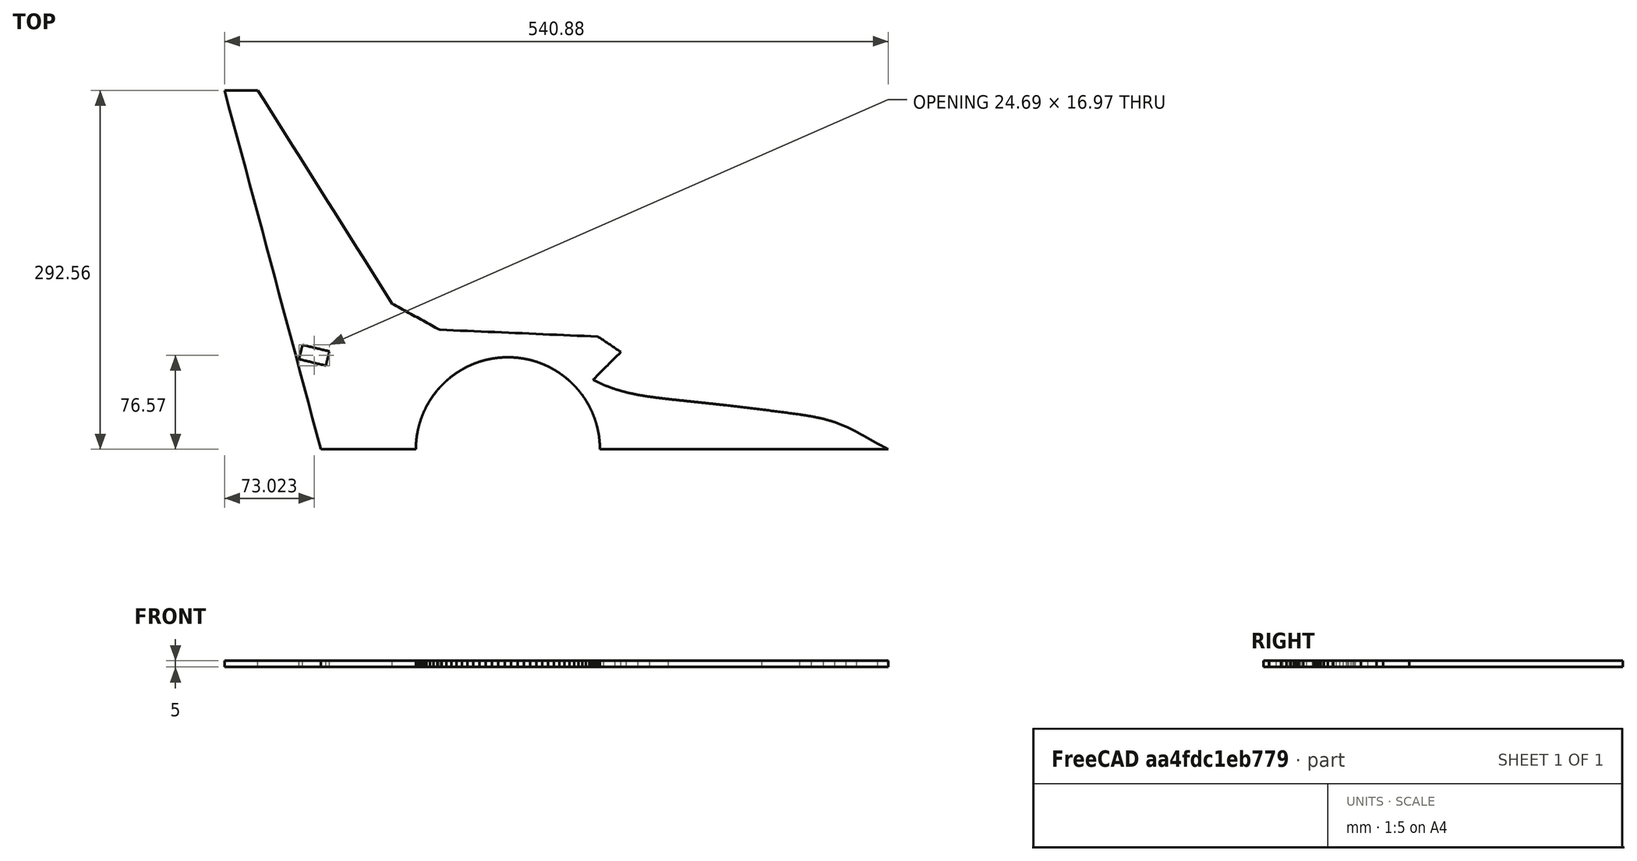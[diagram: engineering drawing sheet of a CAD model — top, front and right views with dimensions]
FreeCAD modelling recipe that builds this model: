
FCSTD DOCUMENT  (FreeCAD 0.19R)
Label: F-35_v2_parts_3
License: All rights reserved
LicenseURL: http://en.wikipedia.org/wiki/All_rights_reserved
objects: App::DocumentObjectGroup×2, PartDesign::CoordinateSystem×2, App::FeaturePython×1, Sketcher::SketchObject×1, PartDesign::Pad×1, PartDesign::Body×1, App::Part×1
note: 6 computed .brp shape members not serialized (recipe doc carries the construction recipe); baked Part::Feature solids carry a one-line shape summary decoded from their .brp

FEATURE [App::DocumentObjectGroup] Parts
FEATURE [PartDesign::CoordinateSystem] LCS_Origin
  AttacherType = Attacher::AttachEngine3D
  MapMode = 2
  Support = -> [X_Axis]
FEATURE [App::DocumentObjectGroup] Constraints
FEATURE [App::FeaturePython] Variables  # WARN: FeaturePython — macro-defined, semantics opaque (R4)
FEATURE [Sketcher::SketchObject] Sketch002
  FullyConstrained = false
  sketch-geometry (77):
    g0: BSplineCurve PolesCount=2 KnotsCount=2 Degree=1 IsPeriodic=0
    g1: BSplineCurve PolesCount=2 KnotsCount=2 Degree=1 IsPeriodic=0
    g2: BSplineCurve PolesCount=2 KnotsCount=2 Degree=1 IsPeriodic=0
    g3: BSplineCurve PolesCount=2 KnotsCount=2 Degree=1 IsPeriodic=0
    g4: BSplineCurve PolesCount=2 KnotsCount=2 Degree=1 IsPeriodic=0
    g5: BSplineCurve PolesCount=2 KnotsCount=2 Degree=1 IsPeriodic=0
    g6: BSplineCurve PolesCount=2 KnotsCount=2 Degree=1 IsPeriodic=0
    g7: BSplineCurve PolesCount=2 KnotsCount=2 Degree=1 IsPeriodic=0
    g8: BSplineCurve PolesCount=2 KnotsCount=2 Degree=1 IsPeriodic=0
    g9: BSplineCurve PolesCount=2 KnotsCount=2 Degree=1 IsPeriodic=0
    g10: BSplineCurve PolesCount=2 KnotsCount=2 Degree=1 IsPeriodic=0
    g11: BSplineCurve PolesCount=2 KnotsCount=2 Degree=1 IsPeriodic=0
    g12: BSplineCurve PolesCount=2 KnotsCount=2 Degree=1 IsPeriodic=0
    g13: BSplineCurve PolesCount=2 KnotsCount=2 Degree=1 IsPeriodic=0
    g14: BSplineCurve PolesCount=2 KnotsCount=2 Degree=1 IsPeriodic=0
    g15: BSplineCurve PolesCount=2 KnotsCount=2 Degree=1 IsPeriodic=0
    g16: BSplineCurve PolesCount=2 KnotsCount=2 Degree=1 IsPeriodic=0
    g17: BSplineCurve PolesCount=2 KnotsCount=2 Degree=1 IsPeriodic=0
    g18: BSplineCurve PolesCount=2 KnotsCount=2 Degree=1 IsPeriodic=0
    g19: BSplineCurve PolesCount=2 KnotsCount=2 Degree=1 IsPeriodic=0
    g20: BSplineCurve PolesCount=2 KnotsCount=2 Degree=1 IsPeriodic=0
    g21: BSplineCurve PolesCount=2 KnotsCount=2 Degree=1 IsPeriodic=0
    g22: BSplineCurve PolesCount=2 KnotsCount=2 Degree=1 IsPeriodic=0
    g23: BSplineCurve PolesCount=2 KnotsCount=2 Degree=1 IsPeriodic=0
    g24: BSplineCurve PolesCount=2 KnotsCount=2 Degree=1 IsPeriodic=0
    g25: BSplineCurve PolesCount=2 KnotsCount=2 Degree=1 IsPeriodic=0
    g26: BSplineCurve PolesCount=2 KnotsCount=2 Degree=1 IsPeriodic=0
    g27: BSplineCurve PolesCount=2 KnotsCount=2 Degree=1 IsPeriodic=0
    g28: BSplineCurve PolesCount=2 KnotsCount=2 Degree=1 IsPeriodic=0
    g29: BSplineCurve PolesCount=2 KnotsCount=2 Degree=1 IsPeriodic=0
    g30: BSplineCurve PolesCount=2 KnotsCount=2 Degree=1 IsPeriodic=0
    g31: BSplineCurve PolesCount=2 KnotsCount=2 Degree=1 IsPeriodic=0
    g32: BSplineCurve PolesCount=2 KnotsCount=2 Degree=1 IsPeriodic=0
    g33: BSplineCurve PolesCount=2 KnotsCount=2 Degree=1 IsPeriodic=0
    g34: BSplineCurve PolesCount=2 KnotsCount=2 Degree=1 IsPeriodic=0
    g35: BSplineCurve PolesCount=2 KnotsCount=2 Degree=1 IsPeriodic=0
    g36: BSplineCurve PolesCount=2 KnotsCount=2 Degree=1 IsPeriodic=0
    g37: BSplineCurve PolesCount=2 KnotsCount=2 Degree=1 IsPeriodic=0
    g38: BSplineCurve PolesCount=2 KnotsCount=2 Degree=1 IsPeriodic=0
    g39: BSplineCurve PolesCount=2 KnotsCount=2 Degree=1 IsPeriodic=0
    g40: BSplineCurve PolesCount=2 KnotsCount=2 Degree=1 IsPeriodic=0
    g41: BSplineCurve PolesCount=2 KnotsCount=2 Degree=1 IsPeriodic=0
    g42: BSplineCurve PolesCount=2 KnotsCount=2 Degree=1 IsPeriodic=0
    g43: BSplineCurve PolesCount=2 KnotsCount=2 Degree=1 IsPeriodic=0
    g44: BSplineCurve PolesCount=2 KnotsCount=2 Degree=1 IsPeriodic=0
    g45: BSplineCurve PolesCount=2 KnotsCount=2 Degree=1 IsPeriodic=0
    g46: BSplineCurve PolesCount=2 KnotsCount=2 Degree=1 IsPeriodic=0
    g47: BSplineCurve PolesCount=2 KnotsCount=2 Degree=1 IsPeriodic=0
    g48: BSplineCurve PolesCount=2 KnotsCount=2 Degree=1 IsPeriodic=0
    g49: BSplineCurve PolesCount=2 KnotsCount=2 Degree=1 IsPeriodic=0
    g50: BSplineCurve PolesCount=2 KnotsCount=2 Degree=1 IsPeriodic=0
    g51: BSplineCurve PolesCount=2 KnotsCount=2 Degree=1 IsPeriodic=0
    g52: BSplineCurve PolesCount=2 KnotsCount=2 Degree=1 IsPeriodic=0
    g53: BSplineCurve PolesCount=2 KnotsCount=2 Degree=1 IsPeriodic=0
    g54: BSplineCurve PolesCount=2 KnotsCount=2 Degree=1 IsPeriodic=0
    g55: BSplineCurve PolesCount=2 KnotsCount=2 Degree=1 IsPeriodic=0
    g56: BSplineCurve PolesCount=2 KnotsCount=2 Degree=1 IsPeriodic=0
    g57: BSplineCurve PolesCount=2 KnotsCount=2 Degree=1 IsPeriodic=0
    g58: BSplineCurve PolesCount=2 KnotsCount=2 Degree=1 IsPeriodic=0
    g59: BSplineCurve PolesCount=2 KnotsCount=2 Degree=1 IsPeriodic=0
    g60: BSplineCurve PolesCount=2 KnotsCount=2 Degree=1 IsPeriodic=0
    g61: BSplineCurve PolesCount=2 KnotsCount=2 Degree=1 IsPeriodic=0
    g62: BSplineCurve PolesCount=2 KnotsCount=2 Degree=1 IsPeriodic=0
    g63: BSplineCurve PolesCount=2 KnotsCount=2 Degree=1 IsPeriodic=0
    g64: BSplineCurve PolesCount=2 KnotsCount=2 Degree=1 IsPeriodic=0
    g65: BSplineCurve PolesCount=2 KnotsCount=2 Degree=1 IsPeriodic=0
    g66: BSplineCurve PolesCount=2 KnotsCount=2 Degree=1 IsPeriodic=0
    g67: BSplineCurve PolesCount=2 KnotsCount=2 Degree=1 IsPeriodic=0
    g68: BSplineCurve PolesCount=2 KnotsCount=2 Degree=1 IsPeriodic=0
    g69: BSplineCurve PolesCount=2 KnotsCount=2 Degree=1 IsPeriodic=0
    g70: BSplineCurve PolesCount=2 KnotsCount=2 Degree=1 IsPeriodic=0
    g71: BSplineCurve PolesCount=2 KnotsCount=2 Degree=1 IsPeriodic=0
    g72: BSplineCurve PolesCount=2 KnotsCount=2 Degree=1 IsPeriodic=0
    g73: BSplineCurve PolesCount=2 KnotsCount=2 Degree=1 IsPeriodic=0
    g74: BSplineCurve PolesCount=2 KnotsCount=2 Degree=1 IsPeriodic=0
    g75: BSplineCurve PolesCount=2 KnotsCount=2 Degree=1 IsPeriodic=0
    g76: BSplineCurve PolesCount=2 KnotsCount=2 Degree=1 IsPeriodic=0
  constraints (62):
    c: Coincident(g6,g7)
    c: Coincident(g7,g8)
    c: Coincident(g8,g9)
    c: Coincident(g9,g10)
    c: Coincident(g10,g11)
    c: Coincident(g11,g12)
    c: Coincident(g12,g13)
    c: Coincident(g13,g14)
    c: Coincident(g14,g15)
    c: Coincident(g15,g16)
    c: Coincident(g16,g17)
    c: Coincident(g17,g18)
    c: Coincident(g18,g19)
    c: Coincident(g19,g20)
    c: Coincident(g20,g21)
    c: Coincident(g21,g22)
    c: Coincident(g22,g23)
    c: Coincident(g23,g24)
    c: Coincident(g25,g26)
    c: Coincident(g26,g27)
    c: Coincident(g27,g28)
    c: Coincident(g28,g29)
    c: Coincident(g29,g30)
    c: Coincident(g30,g31)
    c: Coincident(g31,g32)
    c: Coincident(g32,g33)
    c: Coincident(g33,g34)
    c: Coincident(g34,g35)
    c: Coincident(g35,g36)
    c: Coincident(g36,g37)
    c: Coincident(g37,g38)
    c: Coincident(g38,g39)
    c: Coincident(g39,g40)
    c: Coincident(g40,g41)
    c: Coincident(g41,g42)
    c: Coincident(g42,g43)
    c: Coincident(g43,g44)
    c: Coincident(g44,g45)
    c: Coincident(g45,g46)
    c: Coincident(g46,g47)
    c: Coincident(g47,g48)
    c: Coincident(g48,g49)
    c: Coincident(g49,g50)
    c: Coincident(g50,g51)
    c: Coincident(g51,g52)
    c: Coincident(g52,g53)
    c: Coincident(g53,g54)
    c: Coincident(g54,g55)
    c: Coincident(g55,g56)
    c: Coincident(g56,g57)
    c: Coincident(g57,g58)
    c: Coincident(g58,g59)
    c: Coincident(g59,g60)
    c: Coincident(g60,g61)
    c: Coincident(g61,g62)
    c: Coincident(g62,g63)
    c: Coincident(g63,g64)
    c: Coincident(g64,g65)
    c: Coincident(g65,g66)
    c: Coincident(g66,g67)
    c: Coincident(g67,g68)
    c: Coincident(g68,g69)
FEATURE [PartDesign::Pad] Pad002
  Direction = (1,1,1)
  Length = 5
  Length2 = 100
  Profile = -> Sketch002
  Type = 0
FEATURE [PartDesign::Body] Body002  label="Part3"
  Group = -> [Sketch002,Pad002]
  Origin = -> Origin003
  Tip = -> Pad002
FEATURE [PartDesign::CoordinateSystem] LCS_1
  AttacherType = Attacher::AttachEngine3D
  MapMode = 7
  Placement = pos=(410.681,-413.86,0) rot=(0,1,0;3.14159rad)
  Support = -> [Pad002]
FEATURE [App::Part] Model
  Configuration = 0
  Group = -> [LCS_Origin,Constraints,Variables,Body002,LCS_1]
  Origin = -> Origin
  Type = Assembly4 Model
